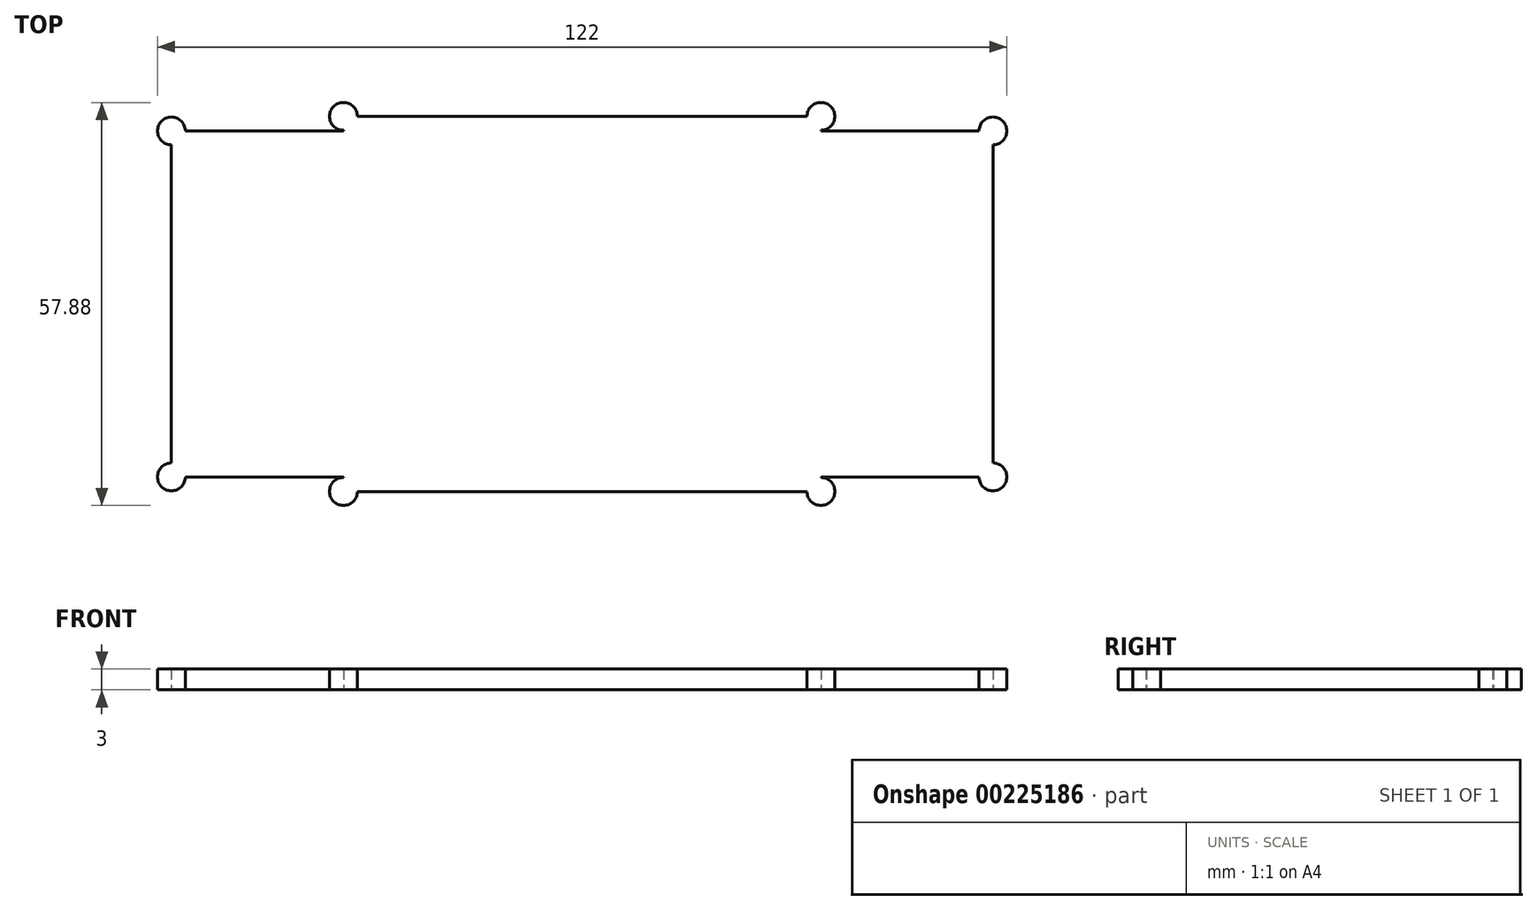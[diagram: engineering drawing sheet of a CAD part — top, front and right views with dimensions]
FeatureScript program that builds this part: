
annotation { "Feature Type Name" : "Feature", "Feature Type Description" : "" }
export const myFeature = defineFeature(function(context is Context, id is Id, definition is map)
    precondition{}
    {
        {
            var Q0;
            Q0=qCreatedBy(makeId("Top.planeOp"),FACE);
            var sketch = newSketch(context, id + "F0", { "sketchPlane" : qUnion([Q0])});
            skLineSegment(sketch, "E0.bottom", {"start": v(59, 24.85) * mm, "end": v(-59, 24.85) * mm});
            skLineSegment(sketch, "E0.top", {"start": v(59, -24.85) * mm, "end": v(-59, -24.85) * mm});
            skLineSegment(sketch, "E0.left", {"start": v(59, 24.85) * mm, "end": v(59, -24.85) * mm});
            skLineSegment(sketch, "E0.right", {"start": v(-59, 24.85) * mm, "end": v(-59, -24.85) * mm});
            skPoint(sketch, "E0.middle", {"position": v(0, 0) * mm});
            skLineSegment(sketch, "E1.bottom", {"start": v(34.3, 26.94) * mm, "end": v(-34.3, 26.94) * mm});
            skLineSegment(sketch, "E1.top", {"start": v(34.3, -26.94) * mm, "end": v(-34.29, -26.94) * mm});
            skLineSegment(sketch, "E1.left", {"start": v(34.3, 26.94) * mm, "end": v(34.3, -26.94) * mm});
            skLineSegment(sketch, "E1.right", {"start": v(-34.29, 26.94) * mm, "end": v(-34.29, -26.94) * mm});
            skCircle(sketch, "E2", {"center": v(-34.3, 26.94) * mm, "radius": 2 * mm});
            skCircle(sketch, "E3", {"center": v(34.3, 26.94) * mm, "radius": 2 * mm});
            skCircle(sketch, "E4", {"center": v(34.3, -26.94) * mm, "radius": 2 * mm});
            skCircle(sketch, "E5", {"center": v(59, -24.85) * mm, "radius": 2 * mm});
            skCircle(sketch, "E6", {"center": v(59, 24.85) * mm, "radius": 2 * mm});
            skCircle(sketch, "E7", {"center": v(-59, 24.85) * mm, "radius": 2 * mm});
            skCircle(sketch, "E8", {"center": v(-59, -24.85) * mm, "radius": 2 * mm});
            skCircle(sketch, "E9", {"center": v(-34.29, -26.94) * mm, "radius": 2 * mm});
            skSolve(sketch);
        }
        {
            var Q0;
            Q0 = qSketchRegion(id + "F0", true);
            extrude(context, id + "F1", {"entities" : qUnion([Q0]), "depth" : 3 * mm});
        }
    });
